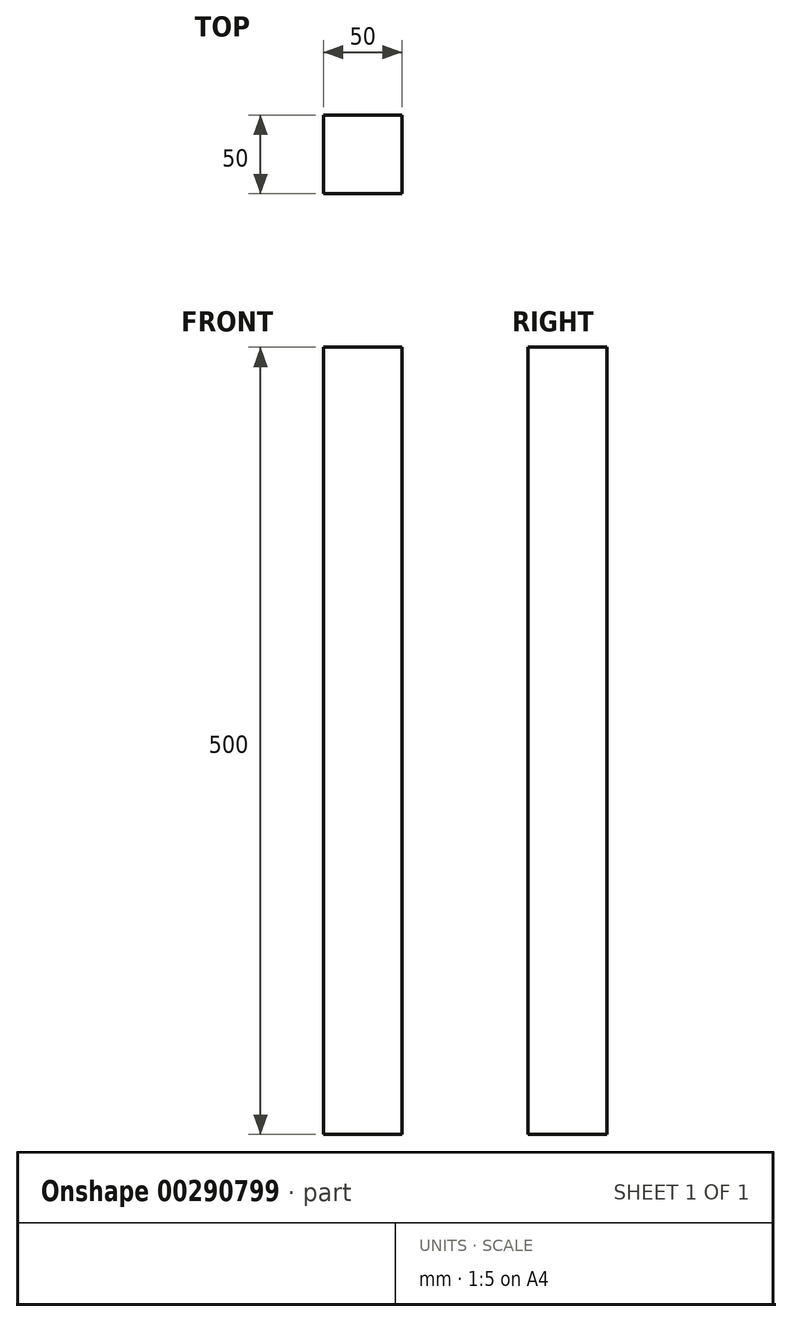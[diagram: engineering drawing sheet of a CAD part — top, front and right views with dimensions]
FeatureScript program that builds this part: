
annotation { "Feature Type Name" : "Feature", "Feature Type Description" : "" }
export const myFeature = defineFeature(function(context is Context, id is Id, definition is map)
    precondition{}
    {
        {
            var Q0;
            Q0=qCreatedBy(makeId("Top.planeOp"),FACE);
            var sketch = newSketch(context, id + "F0", { "sketchPlane" : qUnion([Q0])});
            skLineSegment(sketch, "E0.bottom", {"start": v(25, -25) * mm, "end": v(-25, -25) * mm});
            skLineSegment(sketch, "E0.top", {"start": v(25, 25) * mm, "end": v(-25, 25) * mm});
            skLineSegment(sketch, "E0.left", {"start": v(25, -25) * mm, "end": v(25, 25) * mm});
            skLineSegment(sketch, "E0.right", {"start": v(-25, -25) * mm, "end": v(-25, 25) * mm});
            skPoint(sketch, "E0.middle", {"position": v(0, 0) * mm});
            skSolve(sketch);
        }
        {
            var Q0;
            Q0 = qSketchRegion(id + "F0", true);
            extrude(context, id + "F1", {"entities" : qUnion([Q0]), "depth" : 500 * mm});
        }
    });
